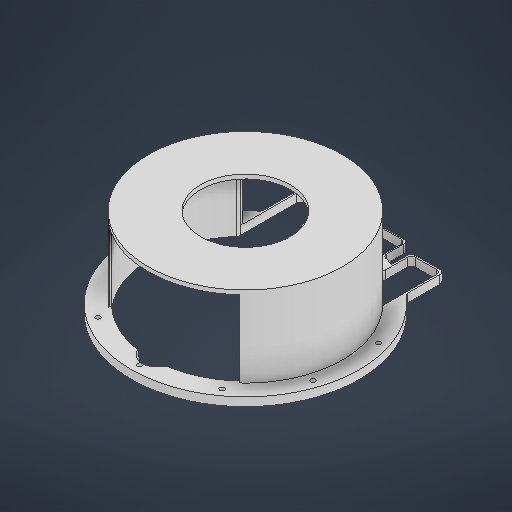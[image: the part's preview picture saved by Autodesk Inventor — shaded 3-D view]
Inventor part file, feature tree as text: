
AUTODESK INVENTOR PART (.ipt)
format: ipt  version: 2025 (Build 290162000, 162)  size: 404,992 bytes
history: native  units: in
note: dims shown in document units (in); Inventor stores cm internally (conversion verified against a paired STEP export)
features: extrude x8, sketch x7, plane x3, fillet x1
ambient origin geometry x8: Origin, YZ Plane, XZ Plane, XY Plane, X Axis, Y Axis, Z Axis, Center Point
bodies: Solid1 (feature_tree)
feature tree (19):
  sketch  "Sketch1"  dims[d5=0.0in d7=0.0in]
  extrude  "Extrusion1"  TaperAngle=0.0deg  [1 undecoded]
  extrude  "Extrusion2"  Depth=4.5276in
  extrude  "Extrusion7"  Depth=2.5591in
  sketch  "Sketch24"  dims[d237=0.0591in d238=2.564in]
  extrude  "Extrusion30"  Depth=2.564in
  extrude  "Extrusion31"  Depth=10.6299in
  extrude  "Extrusion32"  Depth=0.5433in
  extrude  "Extrusion34"  Depth=0.1969in
  sketch  "Sketch30"  dims[d242=2.7608in d243=0.5433in]
  plane  "Work Plane19"
  plane  "Work Plane22"
  extrude  "Extrusion36"  Depth=0.1969in
  fillet  "Fillet19"  Radius=3.6614in
  sketch  "Sketch2"  dims[d18=0.0in d52=4.5276in]
  sketch  "Sketch Circular Pattern5"  dims[d234=0.0787in d235=2.5591in]
  sketch  "Sketch28"  dims[d240=0.8253in d241=10.6299in]
  plane  "Work Plane21"
  sketch  "Sketch31"  dims[d244=1.5298in d247=0.0787in d248=3.5433in d249=3.6614in d250=0.0in d251=3.6614in d252=0.0in d253=9.4488in d254=0.3937in d255=0.0in d264=9.8425in d265=0.2165in d266=3.937in d268=360.0deg d270=1.7955in d271=6.1024in d272=3.937in d273=4.1535in d274=0.0in d282=0.1598in d284=0.7851in d285=3.937in d286=1.4567in d287=2.0812in d288=0.0in d289=3.5039in d290=0.1969in d113=0.0197in d114=0.0344in d115=0.0197in d116=0.0344in d167=0.0197in d168=0.0344in d169=0.0197in d170=0.0344in d215=0.0197in d216=0.0344in d217=0.0197in d218=0.0344in d219=0.0in d220=0.0in d256=0.0197in d257=0.0344in]
note: 1 required parameter value undecoded (feature->parameter linkage not recoverable at this tier; creation-order binding heuristic only, values carry confidence <= 0.55)
